# Revit family: Deca_Torneira_Link_1167.C.LNK
name_source: partatom
category: Plumbing Fixtures
revit_build: Autodesk Revit Architecture 2012 (Build: 20110916_2132(x64)
units: mm (PartAtom-declared; Revit-internal decimal feet)

## types (1)
- 1167.C.LNK
    Acompanha o Produto = Não Aplicável
    Aprovado por = Contino/quattroD
    Atendimento ao Cliente = 0800-011-7073
    CWFU = 0
    Criador por = Contino/quattroD
    Código = 1167.C.LNK
    Default Elevation = 0 mm  [stored 0 ft]
    Description = Torneira de cozinha
    Descrição = Torneira de cozinha
    Diâmetro Água Fria = 15 mm  [stored 0.0492126 ft]
    Fabricante = Deca
    Flow Pressure = 0.00 psi
    HWFU = 0
    Informações Complementares = Bica Alta / Pode ser utilizado com arejadores de vazão constante 6 L/min (código 4224.000)
    Linha = Link
    Louça/Metais = Metais
    Manufacturer = Deca
    Material = Latão Cromado e Plásticos de Engenharia
    Model = 1167.C.LNK
    Norma = NBR 15748
    Peso Liquido (Kg) = 1.143
    Pressão = 2 a 40 mca
    Produto = Torneira de cozinha mesa linha Link
    Raio Água Fria = 8 mm  [stored 0.0262467 ft]
    Segmento = Médio
    Torneira = Deca CR10 Cromado Metal
    URL = www.deca.com.br
    Vendido Separadamente = Ligação flexível (4607.C.030 / 4607.C.040 / 4607.C.050) e Válvula de escoamento

note: [stored X ft] marks values corroborated as IEEE doubles in the binary element streams (Revit-internal decimal feet)

## geometry (parser evidence)
native form markers: Blend x2, Sweep x1
no freeform markers — native parametric forms only
